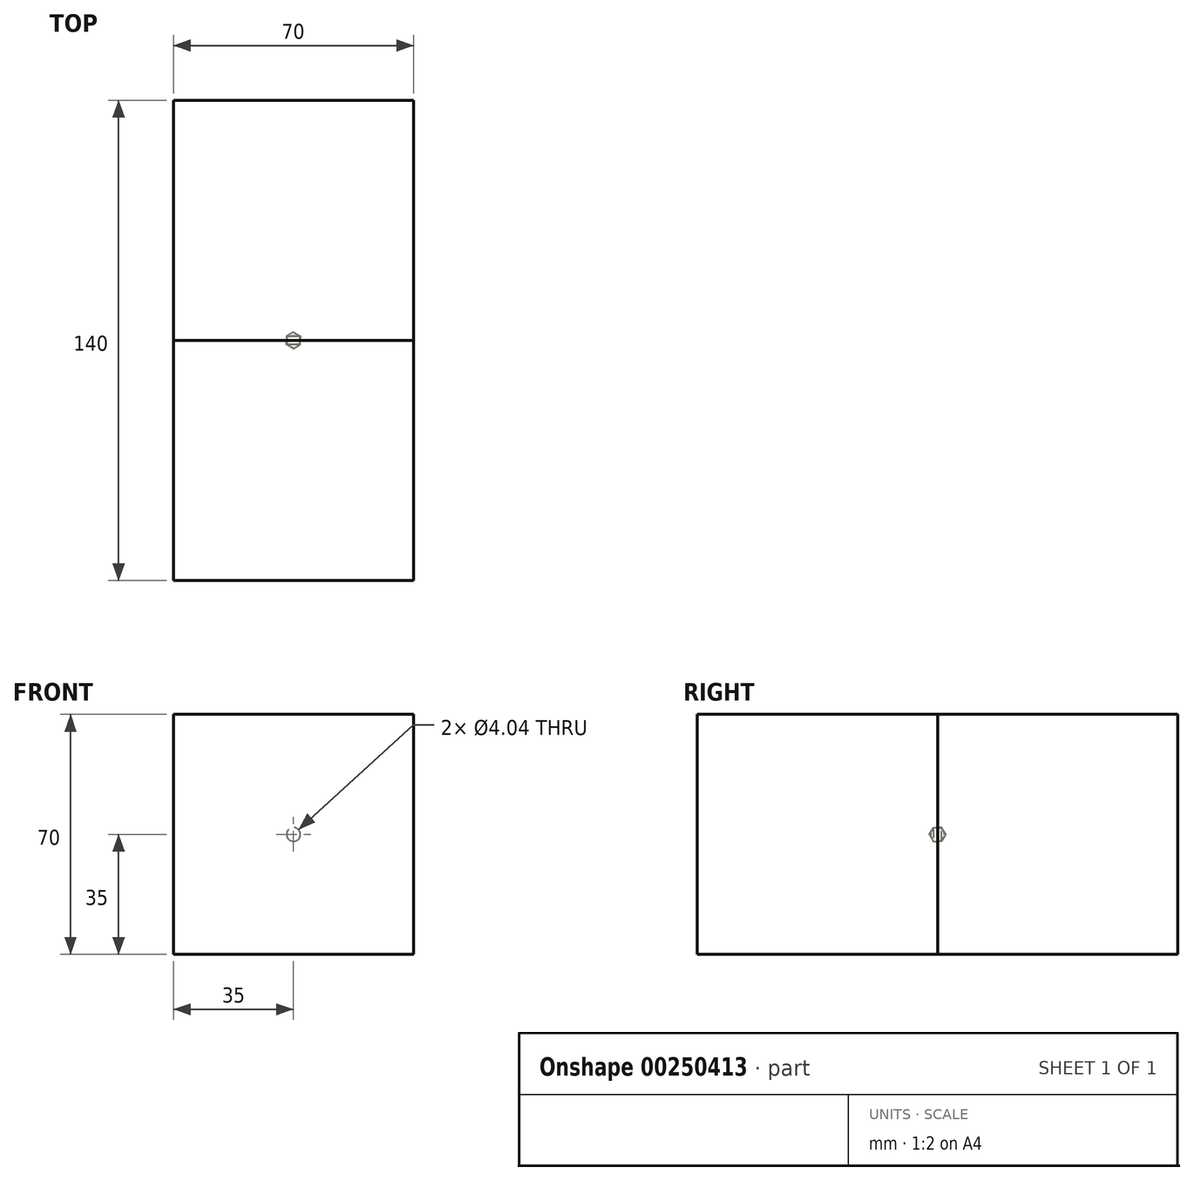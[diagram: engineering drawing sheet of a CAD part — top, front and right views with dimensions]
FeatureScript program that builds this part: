
annotation { "Feature Type Name" : "Feature", "Feature Type Description" : "" }
export const myFeature = defineFeature(function(context is Context, id is Id, definition is map)
    precondition{}
    {
        {
            var Q0;
            Q0=qCreatedBy(makeId("Front.planeOp"),FACE);
            var sketch = newSketch(context, id + "F0", { "sketchPlane" : qUnion([Q0])});
            skArc(sketch, "E0", {"start": v(2, 0) * mm, "mid": v(0, 2) * mm, "end": v(-2, 0) * mm});
            skLineSegment(sketch, "E1", {"start": v(-2, 0) * mm, "end": v(2, 0) * mm});
            skSolve(sketch);
        }
        {
            var Q0;
            Q0=makeQuery(id+"F0.imprint","IMPRINT",FACE,{"disambiguationData":[TD([[makeQuery(id+"F0.imprint","IMPRINT",EDGE,{"derivedFrom":sQuery(id+"F0.wireOp",EDGE,"E0")}),1.0]])]});
            var Q1;
            Q1=sQuery(id+"F0.wireOp",EDGE,"E1");
            revolve(context, id + "F1", {"entities" : qUnion([Q0]), "axis" : qUnion([Q1]), "revolveType" : RevolveType.FULL});
        }
        {
            var Q0;
            Q0=qCreatedBy(makeId("Front.planeOp"),FACE);
            var sketch = newSketch(context, id + "F2", { "sketchPlane" : qUnion([Q0])});
            skLineSegment(sketch, "E2.bottom", {"start": v(35, 35) * mm, "end": v(-35, 35) * mm});
            skLineSegment(sketch, "E2.top", {"start": v(35, -35) * mm, "end": v(-35, -35) * mm});
            skLineSegment(sketch, "E2.left", {"start": v(35, 35) * mm, "end": v(35, -35) * mm});
            skLineSegment(sketch, "E2.right", {"start": v(-35, 35) * mm, "end": v(-35, -35) * mm});
            skPoint(sketch, "E2.middle", {"position": v(0, 0) * mm});
            skCircle(sketch, "E3", {"center": v(0, 0) * mm, "radius": 2 * mm});
            skSolve(sketch);
        }
        {
            var Q0;
            Q0=makeQuery(id+"F2.imprint","IMPRINT",FACE,{"disambiguationData":[TD([[makeQuery(id+"F2.imprint","IMPRINT",EDGE,{"derivedFrom":sQuery(id+"F2.wireOp",EDGE,"E2.bottom")}),1.0]])]});
            var Q1;
            Q1=makeQuery(id+"F2.imprint","IMPRINT",FACE,{"disambiguationData":[TD([[makeQuery(id+"F2.imprint","IMPRINT",EDGE,{"derivedFrom":sQuery(id+"F2.wireOp",EDGE,"E3")}),1.0]])]});
            extrude(context, id + "F3", {"entities" : qUnion([Q0, Q1]), "depth" : 70 * mm});
        }
        {
            var Q0;
            Q0=sQuery(id+"F2.wireOp",VERTEX,"E2.middle");
            var Q1;
            Q1=makeQuery(id+"F3.opExtrude","SWEPT_BODY",BODY,{"disambiguationData":[OSD([sQuery(id+"F2.wireOp",EDGE,"E2.bottom"),sQuery(id+"F2.wireOp",EDGE,"E2.top"),sQuery(id+"F2.wireOp",EDGE,"E2.left"),sQuery(id+"F2.wireOp",EDGE,"E2.right")])]});
            hole(context, id + "F4", {"style" : HoleStyle.SIMPLE, "endStyle" : HoleEndStyle.BLIND, "oppositeDirection" : true, "standardTappedOrClearance" : lookupTablePath({ "standard" : "ANSI", "size" : "#21 (0.16)", "type" : "Drilled" }), "standardBlindInLast" : lookupTablePath({ "standard" : "ANSI", "size" : "#21", "type" : "Drilled" }), "holeDiameter" : 4.04 * mm, "holeDepth" : 1.2 * mm, "tappedDepth" : 12 * mm, "tapClearance" : 3, "locations" : qUnion([Q0]), "scope" : qUnion([Q1])});
        }
        {
            var Q0;
            Q0=makeQuery(id+"F2.imprint","IMPRINT",FACE,{"disambiguationData":[TD([[makeQuery(id+"F2.imprint","IMPRINT",EDGE,{"derivedFrom":sQuery(id+"F2.wireOp",EDGE,"E2.bottom")}),1.0]])]});
            var sketch = newSketch(context, id + "F5", { "sketchPlane" : qUnion([Q0])});
            skLineSegment(sketch, "E4.bottom", {"start": v(-35, -35) * mm, "end": v(35, -35) * mm});
            skLineSegment(sketch, "E4.top", {"start": v(-35, 35) * mm, "end": v(35, 35) * mm});
            skLineSegment(sketch, "E4.left", {"start": v(-35, -35) * mm, "end": v(-35, 35) * mm});
            skLineSegment(sketch, "E4.right", {"start": v(35, -35) * mm, "end": v(35, 35) * mm});
            skPoint(sketch, "E4.middle", {"position": v(0, 0) * mm});
            skSolve(sketch);
        }
        {
            var Q0;
            Q0=makeQuery(id+"F5.imprint","IMPRINT",FACE,{"disambiguationData":[TD([[makeQuery(id+"F5.imprint","IMPRINT",EDGE,{"derivedFrom":sQuery(id+"F5.wireOp",EDGE,"E4.bottom")}),-1.0]])]});
            var Q1;
            Q1=makeQuery(id+"F5.imprint","IMPRINT",FACE,{"disambiguationData":[TD([[makeQuery(id+"F5.imprint","IMPRINT",EDGE,{"derivedFrom":makeQuery(id+"F2.imprint","IMPRINT",EDGE,{"derivedFrom":sQuery(id+"F2.wireOp",EDGE,"E3")})}),1.0]])]});
            extrude(context, id + "F6", {"entities" : qUnion([Q0, Q1]), "oppositeDirection" : true, "depth" : 70 * mm});
        }
        {
            var Q0;
            Q0=sQuery(id+"F2.wireOp",VERTEX,"E2.middle");
            var Q1;
            Q1=makeQuery(id+"F6.opExtrude","SWEPT_BODY",BODY,{"disambiguationData":[OSD([sQuery(id+"F5.wireOp",EDGE,"E4.bottom"),sQuery(id+"F5.wireOp",EDGE,"E4.top"),sQuery(id+"F5.wireOp",EDGE,"E4.left"),sQuery(id+"F5.wireOp",EDGE,"E4.right")])]});
            hole(context, id + "F7", {"style" : HoleStyle.SIMPLE, "endStyle" : HoleEndStyle.BLIND, "standardTappedOrClearance" : lookupTablePath({ "standard" : "ANSI", "size" : "#21 (0.16)", "type" : "Drilled" }), "standardBlindInLast" : lookupTablePath({ "standard" : "ANSI", "size" : "#21", "type" : "Drilled" }), "holeDiameter" : 4.04 * mm, "holeDepth" : 1.2 * mm, "tappedDepth" : 12 * mm, "tapClearance" : 3, "locations" : qUnion([Q0]), "scope" : qUnion([Q1])});
        }
    });
